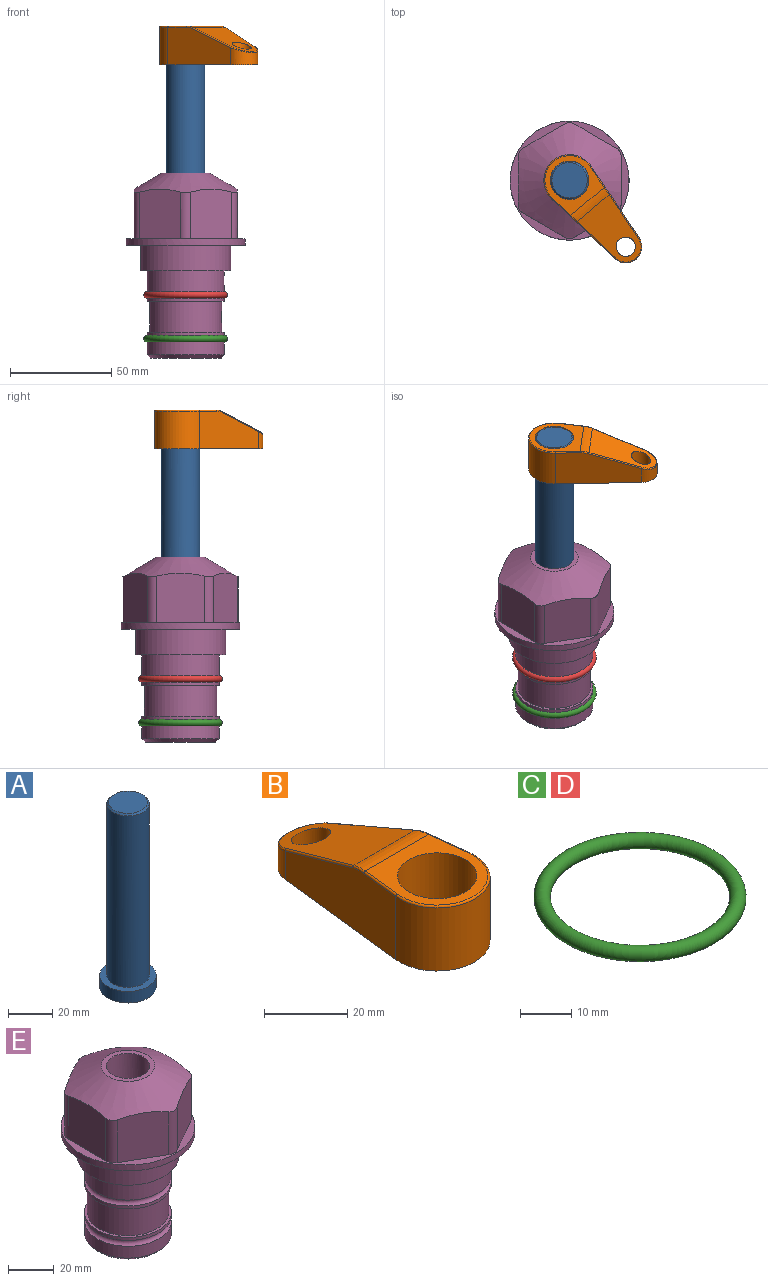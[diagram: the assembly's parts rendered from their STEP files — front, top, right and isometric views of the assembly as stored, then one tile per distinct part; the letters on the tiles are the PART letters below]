
ASSEMBLY  parts=5 mates=3
PART A: 6 faces, bbox 25.4x25.4x101.6 mm
  f0: plane 17.46x17.46mm, normal (0,0,1), area 239.5mm2, adj f5
  f1: plane 25.4x25.4mm, normal (0,0,-1), area 506.7mm2, adj f2
  f2: cylinder r=12.7mm len=25.4mm, axis (0,0,1), area 506.7mm2, adj f1,f3
  f3: plane 25.4x25.4mm, normal (0,0,1), area 221.7mm2, adj f2,f4
  f4: cylinder r=9.53mm len=94.46mm, axis (0,0,1), area 5653mm2, adj f3,f5
  f5: cone r=8.73mm half-angle=45deg, axis (0,0,-1), area 64.4mm2, adj f0,f4
PART B: 44 faces, bbox 27.5x64.5x19.1 mm
  f0: plane 2.3x0.95mm, normal (0,0,-1), area 1mm2, adj f25,f30,f34
  f1: plane 63.5x25.4mm, normal (0,0,-1), area 561.7mm2, adj f2,f3,f4,f5,f6,f7,f19,f20
  f2: cylinder r=12.7mm len=25.4mm, axis (0,0,-1), area 792.2mm2, adj f1,f3,f5,f13
  f3: plane 42.33x18.54mm, normal (0.99,0.11,0), area 647mm2, adj f1,f2,f4,f11,f12,f14
  f4: cylinder r=7.94mm len=15.78mm, axis (0,0,-1), area 158.6mm2, adj f1,f3,f5,f16
  f5: plane 42.33x18.54mm, normal (-0.99,0.11,0), area 647mm2, adj f1,f2,f4,f15,f17,f18
  f6: cylinder r=9.53mm len=19.05mm, axis (0,0,-1), area 1140.1mm2, adj f1,f8
  f7: cylinder r=4.76mm len=10.98mm, axis (0,0,-1), area 276.1mm2, adj f1,f9
  f8: plane 25.83x24.38mm, normal (0,0,1), area 262.2mm2, adj f6,f10,f11,f13,f15
  f9: plane 32.49x20.55mm, normal (0,0.34,0.94), area 489.9mm2, adj f7,f10,f14,f16,f18
  f10: cylinder r=12.7mm len=21.49mm, axis (-1,0,0), area 93.2mm2, adj f8,f9,f12,f17
  f11: cylinder r=0.51mm len=12.34mm, axis (0.11,-0.99,0), area 9.9mm2, adj f3,f8,f12,f13
  f12: bspline ~7.62x1.64mm, area 3.5mm2, adj f3,f10,f11,f14
  f13: torus R=12.19mm, axis (0,0,1), area 33.6mm2, adj f2,f8,f11,f15
  f14: cylinder r=0.51mm len=26.01mm, axis (0.1,-0.93,0.34), area 21.6mm2, adj f3,f9,f12,f16
  f15: cylinder r=0.51mm len=12.34mm, axis (0.11,0.99,0), area 9.9mm2, adj f5,f8,f13,f17
  f16: bspline ~15.78x7.05mm, area 15.7mm2, adj f4,f9,f14,f18
  f17: bspline ~7.62x1.64mm, area 3.5mm2, adj f5,f10,f15,f18
  f18: cylinder r=0.51mm len=26.01mm, axis (0.1,0.93,-0.34), area 21.6mm2, adj f5,f9,f16,f17
  f19: plane 21.6x14.29mm, normal (-0.99,-0.11,0), area 242.6mm2, adj f1,f26,f28,f34,f36,f38
  f20: plane 21.6x14.29mm, normal (0.99,-0.11,0), area 242.6mm2, adj f1,f27,f29,f37,f39,f41
  f21: cylinder r=12.7mm len=14.29mm, axis (0,0,-1), area 173.2mm2, adj f1,f26,f27,f30,f31,f33
  f22: cylinder r=7.94mm len=7.63mm, axis (0,0,-1), area 53.8mm2, adj f1,f28,f29,f42
  f23: plane 2.3x0.95mm, normal (0,0,-1), area 1mm2, adj f25,f33,f37
  f24: plane 17.94x12.32mm, normal (0,-0.34,-0.94), area 191.2mm2, adj f25,f38,f41,f42
  f25: cylinder r=9.53mm len=12.93mm, axis (-1,0,0), area 37.5mm2, adj f0,f23,f24,f31,f36,f39
  f26: cylinder r=1.59mm len=14.29mm, axis (0,0,-1), area 49mm2, adj f1,f19,f21,f32
  f27: cylinder r=1.59mm len=14.29mm, axis (0,0,-1), area 49mm2, adj f1,f20,f21,f35
  f28: cylinder r=1.59mm len=7.28mm, axis (0,0,-1), area 22.1mm2, adj f1,f19,f22,f40
  f29: cylinder r=1.59mm len=7.28mm, axis (0,0,-1), area 22.1mm2, adj f1,f20,f22,f43
  f30: torus R=14.29mm, axis (0,0,1), area 5.8mm2, adj f0,f21,f31,f32
  f31: bspline ~11.06x2.73mm, area 20.8mm2, adj f21,f25,f30,f33
  f32: sphere r=1.59mm, area 5.4mm2, adj f26,f30,f34
  f33: torus R=14.29mm, axis (0,0,1), area 5.8mm2, adj f21,f23,f31,f35
  f34: cylinder r=1.59mm len=1.68mm, axis (-0.11,0.99,0), area 2.4mm2, adj f0,f19,f32,f36
  f35: sphere r=1.59mm, area 5.4mm2, adj f27,f33,f37
  f36: bspline ~5.82x2.33mm, area 7.7mm2, adj f19,f25,f34,f38
  f37: cylinder r=1.59mm len=1.68mm, axis (0.11,0.99,0), area 2.4mm2, adj f20,f23,f35,f39
  f38: cylinder r=1.59mm len=18.33mm, axis (0.1,-0.93,0.34), area 46.7mm2, adj f19,f24,f36,f40
  f39: bspline ~5.82x2.33mm, area 7.7mm2, adj f20,f25,f37,f41
  f40: sphere r=1.59mm, area 3.6mm2, adj f28,f38,f42
  f41: cylinder r=1.59mm len=18.33mm, axis (0.1,0.93,-0.34), area 46.7mm2, adj f20,f24,f39,f43
  f42: bspline ~8.31x1.84mm, area 15.3mm2, adj f22,f24,f40,f43
  f43: sphere r=1.59mm, area 3.6mm2, adj f29,f41,f42
PART C: 1 faces, bbox 44.7x44.7x3.2 mm
  f0: torus R=19.05mm, axis (0,0,1), area 1193.9mm2
PART D: same geometry as C
PART E: 36 faces, bbox 58.7x58.7x91.2 mm
  f0: cylinder r=17.78mm len=35.56mm, axis (0,0,1), area 1670.8mm2, adj f23,f24,f31
  f1: cylinder r=19.05mm len=38.1mm, axis (0,0,1), area 1191.9mm2, adj f26,f27,f30
  f2: plane 58.66x58.66mm, normal (0,0,-1), area 1150.6mm2, adj f3,f28
  f3: cylinder r=29.33mm len=58.66mm, axis (0,0,-1), area 585.1mm2, adj f2,f4
  f4: plane 58.66x58.66mm, normal (0,0,1), area 475.9mm2, adj f3,f5,f6,f7,f8,f9,f10,f11
  f5: plane 24.5x20.32mm, normal (-0.5,0.87,0), area 562.8mm2, adj f4,f15,f16,f17
  f6: plane 24.5x20.32mm, normal (0.5,0.87,0), area 562.8mm2, adj f4,f14,f15,f17
  f7: plane 24.5x23.48mm, normal (1,0,0), area 562.8mm2, adj f4,f13,f14,f17
  f8: plane 24.5x20.32mm, normal (0.5,-0.87,0), area 562.8mm2, adj f4,f12,f13,f17
  f9: plane 24.5x20.32mm, normal (-0.5,-0.87,0), area 562.8mm2, adj f4,f11,f12,f17
  f10: plane 24.5x23.48mm, normal (-1,0,0), area 562.8mm2, adj f4,f11,f16,f17
  f11: cylinder r=5.08mm len=23.01mm, axis (0,0,-1), area 121.2mm2, adj f4,f9,f10,f17
  f12: cylinder r=5.08mm len=23.01mm, axis (0,0,-1), area 121.2mm2, adj f4,f8,f9,f17
  f13: cylinder r=5.08mm len=23.01mm, axis (0,0,-1), area 121.2mm2, adj f4,f7,f8,f17
  f14: cylinder r=5.08mm len=23.01mm, axis (0,0,-1), area 121.2mm2, adj f4,f6,f7,f17
  f15: cylinder r=5.08mm len=23.01mm, axis (0,0,-1), area 121.2mm2, adj f4,f5,f6,f17
  f16: cylinder r=5.08mm len=23.01mm, axis (0,0,-1), area 121.2mm2, adj f4,f5,f10,f17
  f17: cone r=11.73mm half-angle=60deg, axis (0,0,-1), area 2071.8mm2, adj f5,f6,f7,f8,f9,f10,f11,f12
  f18: plane 23.46x23.46mm, normal (0,0,1), area 147.4mm2, adj f17,f35
  f19: plane 34.93x34.93mm, normal (0,0,-1), area 958mm2, adj f29
  f20: cylinder r=19.05mm len=38.1mm, axis (0,0,1), area 760.1mm2, adj f21,f29
  f21: torus R=19.05mm, axis (0,0,1), area 565.3mm2, adj f20,f22
  f22: cylinder r=19.05mm len=38.1mm, axis (0,0,1), area 190mm2, adj f21,f23
  f23: plane 38.1x38.1mm, normal (0,0,1), area 146.9mm2, adj f0,f22
  f24: plane 38.1x38.1mm, normal (0,0,-1), area 146.9mm2, adj f0,f25
  f25: cylinder r=19.05mm len=38.1mm, axis (0,0,1), area 190mm2, adj f24,f26
  f26: torus R=19.05mm, axis (0,0,1), area 565.3mm2, adj f1,f25
  f27: plane 44.45x44.45mm, normal (0,0,-1), area 411.7mm2, adj f1,f28
  f28: cylinder r=22.23mm len=44.45mm, axis (0,0,1), area 1773.5mm2, adj f2,f27
  f29: cone r=19.05mm half-angle=45deg, axis (0,0,1), area 257.5mm2, adj f19,f20
  f30: cylinder r=3.17mm len=6.75mm, axis (-1,0,0), area 128mm2, adj f1,f33
  f31: cylinder r=3.17mm len=6.35mm, axis (-1,0,0), area 102.5mm2, adj f0,f33
  f32: plane 25.4x25.4mm, normal (0,0,1), area 506.7mm2, adj f33
  f33: cylinder r=12.7mm len=66.42mm, axis (0,0,-1), area 5236.2mm2, adj f30,f31,f32,f34
  f34: cone r=9.53mm half-angle=30deg, axis (0,0,-1), area 443.4mm2, adj f33,f35
  f35: cylinder r=9.53mm len=19.05mm, axis (0,0,-1), area 849mm2, adj f18,f34
PLACE A rot(axis=(0,0,-1),49.8deg) t=(0,0,34.41)mm
PLACE B rot(axis=(0,0,-1),139.8deg) t=(0,0,89.02)mm
PLACE C t=(0,0,-21.59)mm
PLACE D at identity
PLACE E at identity fixed
MATE fastened C.f0 <-> E.f0  axis (0,0,1) through (0,0,-46.1)mm
MATE cylindrical A.f2 <-> E.f0  axis (0,0,1) through (0,0,60.05)mm
MATE fastened B.f2 <-> A.f2  axis (0,0,1) through (0,0,108.07)mm
